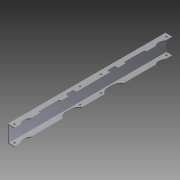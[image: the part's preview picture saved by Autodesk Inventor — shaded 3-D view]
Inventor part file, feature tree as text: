
AUTODESK INVENTOR PART (.ipt)
format: ipt  version: 2012 (Build 160160000, 160)  size: 178,176 bytes
history: native  units: in
note: dims shown in document units (in); Inventor stores cm internally (conversion verified against a paired STEP export)
features: extrude x3, sketch x3, fillet x1
ambient origin geometry x8: Origin, YZ Plane, XZ Plane, XY Plane, X Axis, Y Axis, Z Axis, Center Point
bodies: Solid1 (feature_tree)
feature tree (7):
  extrude  "Extrusion1"  Depth=20.75in TaperAngle=0.0deg
  extrude  "Extrusion2"  Depth=1.5in
  extrude  "Extrusion3"  Depth=0.125in TaperAngle=0.0deg
  fillet  "Fillet1"  Radius=10.375in
  sketch  "Sketch1"  dims[d0=0.125in d1=0.125in d2=0.125in d3=2.25in d4=0.875in d5=20.75in d6=0.0in]
  sketch  "Sketch2"  dims[d7=3.375in d8=2.75in d9=0.25in d10=7.125in d11=1.0in d12=1.0in d13=1.5in d14=0.375in d15=0.25in d16=9.0in d17=1.5in]
  sketch  "Sketch3"  dims[d18=0.45in d19=0.125in d20=0.0in d21=10.375in d22=1.25in d23=0.5in d24=7.375in d25=0.3125in d26=1.5in d27=1.5in d28=1.0in d29=10.375in d30=0.125in d31=0.0in d32=0.125in]
